SOLIDWORKS PART (.sldprt)
format: sldprt  version: not decoded by parser v0  size: 173,568 bytes
history: native  units: mm
features: sketch x8, plane x5, sweep x3, extrude x2, material x1, mirror x1, fillet x1 (+8 scaffold rows collapsed)
feature tree (29):
  scaffold x8  (default folders/planes/origin — collapsed)
  material  "Matériau <non spécifié>"
  plane  "Plan de face"
  plane  "Plan de dessus"
  plane  "Plan de droite"
  sketch  "Esquisse1"
  extrude  "Extrusion2"  Depth=3.6mm
  sketch  "Esquisse2"
  sketch  "Esquisse3"  dims[D4=1.0mm D1=5.0mm D2=4.0mm D3=1.6mm]
  sweep  "Balayage1"
  sketch  "Esquisse4"  dims[D1=0.3mm D2=0.6mm]
  sketch  "Esquisse5"  dims[D1=5.2mm D2=2.0mm D3=2.54mm D4=2.0mm]
  sweep  "Balayage2"
  plane  "Plan1"  Offset=0mm
  plane  "Plan3"  Offset=2.54mm
  sketch  "Esquisse6"  dims[D1=0.4mm D2=0.2mm]
  sketch  "Esquisse7"
  sweep  "Balayage3"
  mirror  "Symétrie1"
  sketch  "Esquisse9"  dims[D2=~1.215634mm D1=3.0mm]
  extrude  "Extrusion3"  Depth=2.2mm
  fillet  "Congé1"  Radius=2.2mm
decode coverage: 8 of 15 modeling features carry decoded parameters
note: ~ marks probable driven/reference dimensions
note: suppression state not decoded; provenance and decode notes live in map.json
